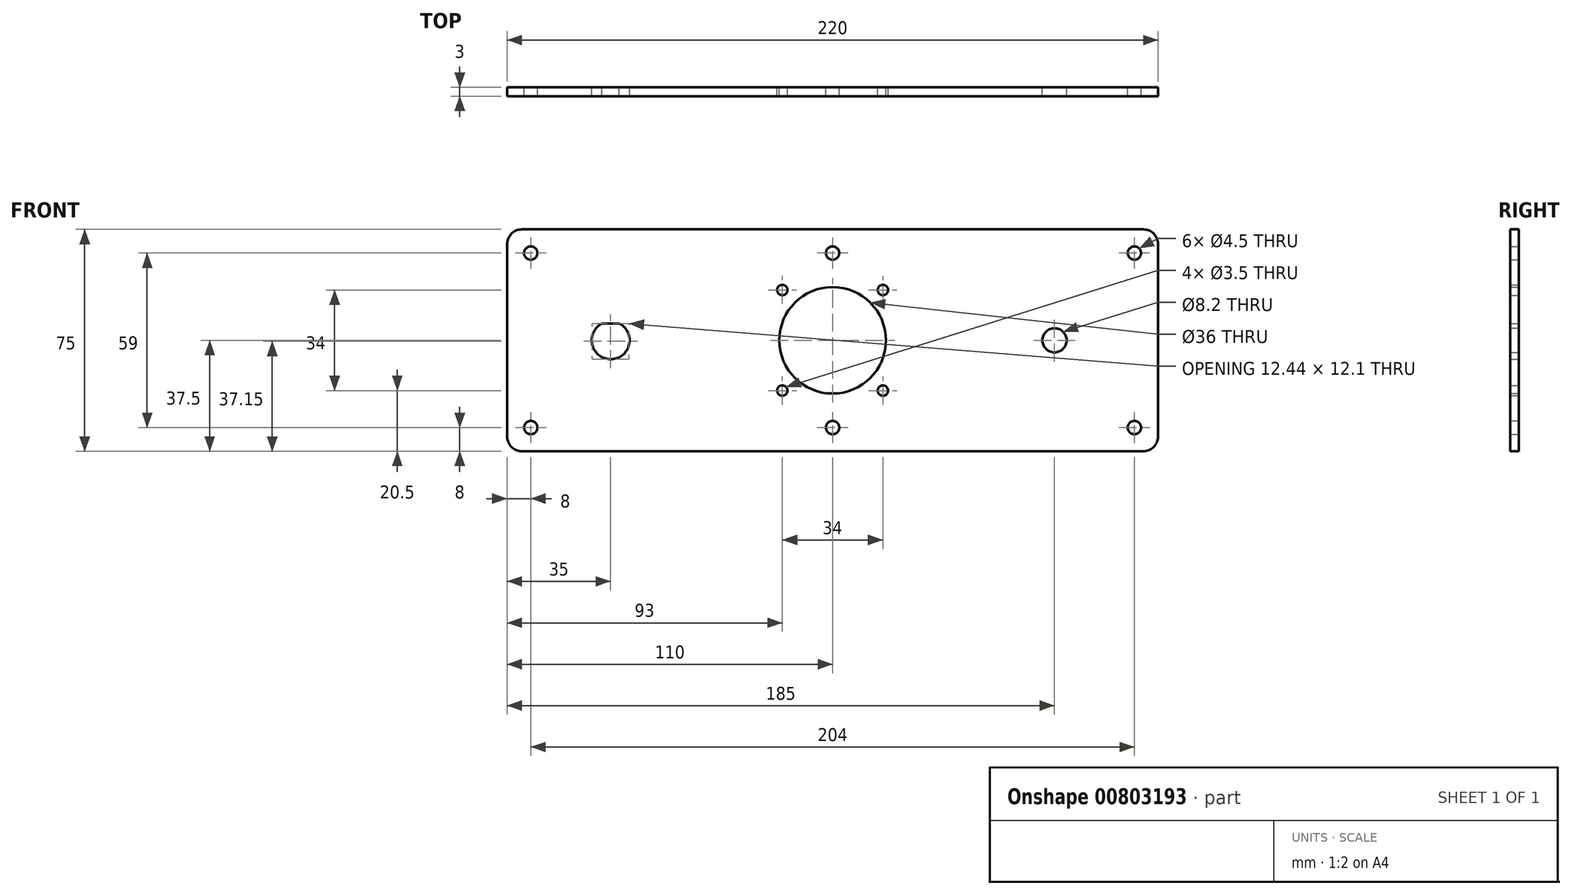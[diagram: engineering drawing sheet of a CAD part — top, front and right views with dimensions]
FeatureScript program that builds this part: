
annotation { "Feature Type Name" : "Feature", "Feature Type Description" : "" }
export const myFeature = defineFeature(function(context is Context, id is Id, definition is map)
    precondition{}
    {
        {
            var Q0;
            Q0=qCreatedBy(makeId("Front.planeOp"),FACE);
            var sketch = newSketch(context, id + "F0", { "sketchPlane" : qUnion([Q0])});
            skPoint(sketch, "E0.middle", {"position": v(0, 0) * mm});
            skArc(sketch, "E1", {"start": v(-77.91, 5.7) * mm, "mid": v(-75, -6.4) * mm, "end": v(-72.09, 5.7) * mm});
            skLineSegment(sketch, "E2", {"start": v(-77.91, 5.7) * mm, "end": v(-72.09, 5.7) * mm});
            skCircle(sketch, "E3", {"center": v(75, 0) * mm, "radius": 4.1 * mm});
            skCircle(sketch, "E4", {"center": v(0, 0) * mm, "radius": 18 * mm});
            skCircle(sketch, "E5", {"center": v(-17, 17) * mm, "radius": 1.75 * mm});
            skCircle(sketch, "E6", {"center": v(-17, -17) * mm, "radius": 1.75 * mm});
            skCircle(sketch, "E7", {"center": v(17, -17) * mm, "radius": 1.75 * mm});
            skCircle(sketch, "E8", {"center": v(17, 17) * mm, "radius": 1.75 * mm});
            skLineSegment(sketch, "E9.bottom", {"start": v(105, 37.5) * mm, "end": v(-105, 37.5) * mm});
            skLineSegment(sketch, "E9.top", {"start": v(105, -37.5) * mm, "end": v(-105, -37.5) * mm});
            skLineSegment(sketch, "E9.left", {"start": v(110, 32.5) * mm, "end": v(110, -32.5) * mm});
            skLineSegment(sketch, "E9.right", {"start": v(-110, 32.5) * mm, "end": v(-110, -32.5) * mm});
            skCircle(sketch, "E10", {"center": v(-102, 29.5) * mm, "radius": 2.25 * mm});
            skCircle(sketch, "E11", {"center": v(102, 29.5) * mm, "radius": 2.25 * mm});
            skCircle(sketch, "E12", {"center": v(102, -29.5) * mm, "radius": 2.25 * mm});
            skCircle(sketch, "E13", {"center": v(-102, -29.5) * mm, "radius": 2.25 * mm});
            skCircle(sketch, "E14", {"center": v(0, 29.5) * mm, "radius": 2.25 * mm});
            skCircle(sketch, "E15", {"center": v(0, -29.5) * mm, "radius": 2.25 * mm});
            skPoint(sketch, "E16.visualSharp", {"position": v(-110, 37.5) * mm});
            skArc(sketch, "E16.filletArc", {"start": v(-105, 37.5) * mm, "mid": v(-108.54, 36.04) * mm, "end": v(-110, 32.5) * mm});
            skPoint(sketch, "E17.visualSharp", {"position": v(-110, -37.5) * mm});
            skArc(sketch, "E17.filletArc", {"start": v(-110, -32.5) * mm, "mid": v(-108.54, -36.04) * mm, "end": v(-105, -37.5) * mm});
            skPoint(sketch, "E18.visualSharp", {"position": v(110, 37.5) * mm});
            skArc(sketch, "E18.filletArc", {"start": v(110, 32.5) * mm, "mid": v(108.54, 36.04) * mm, "end": v(105, 37.5) * mm});
            skPoint(sketch, "E19.visualSharp", {"position": v(110, -37.5) * mm});
            skArc(sketch, "E19.filletArc", {"start": v(105, -37.5) * mm, "mid": v(108.54, -36.04) * mm, "end": v(110, -32.5) * mm});
            skSolve(sketch);
        }
        {
            var Q0;
            Q0=makeQuery(id+"F0.imprint","IMPRINT",FACE,{"disambiguationData":[TD([[makeQuery(id+"F0.imprint","IMPRINT",EDGE,{"derivedFrom":sQuery(id+"F0.wireOp",EDGE,"E1")}),-1.0]])]});
            extrude(context, id + "F1", {"entities" : qUnion([Q0]), "depth" : 3 * mm, "offsetDistance" : 25 * mm});
        }
    });
